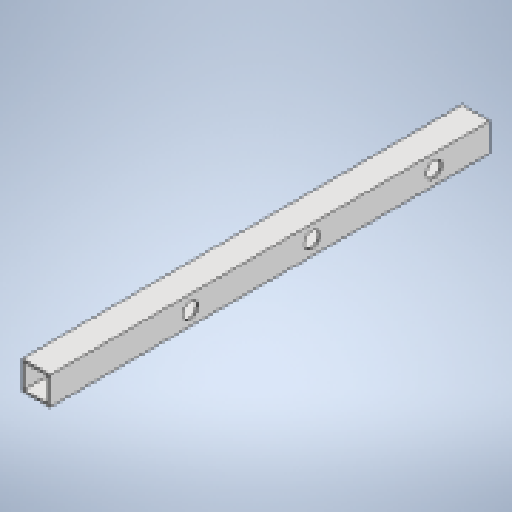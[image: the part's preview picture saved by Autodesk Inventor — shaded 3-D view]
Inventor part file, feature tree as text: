
AUTODESK INVENTOR PART (.ipt)
format: ipt  version: 2025.1 (Build 291241020, 241B)  size: 194,048 bytes
history: native  units: mm
features: extrude x2, sketch x2, projected_geometry x1
ambient origin geometry x8: Origin, YZ Plane, XZ Plane, XY Plane, X Axis, Y Axis, Z Axis, Center Point
bodies: Body1 (feature_tree)
feature tree (5):
  extrude  "Extrusion3"  Depth=30.0mm
  extrude  "Extrusion4"  Depth=2.0mm
  sketch  "Sketch9"  dims[d61=500.0mm d172=30.0mm]
  sketch  "Sketch10"  dims[d173=30.0mm d174=2.0mm d175=400.0mm d176=0.0mm d177=17.0mm d178=17.0mm d179=0.0mm d180=0.0mm d181=30.0mm d182=90.0mm d183=250.0mm d185=400.0mm d186=17.0mm]
  projected_geometry  "Projected Loop3"
